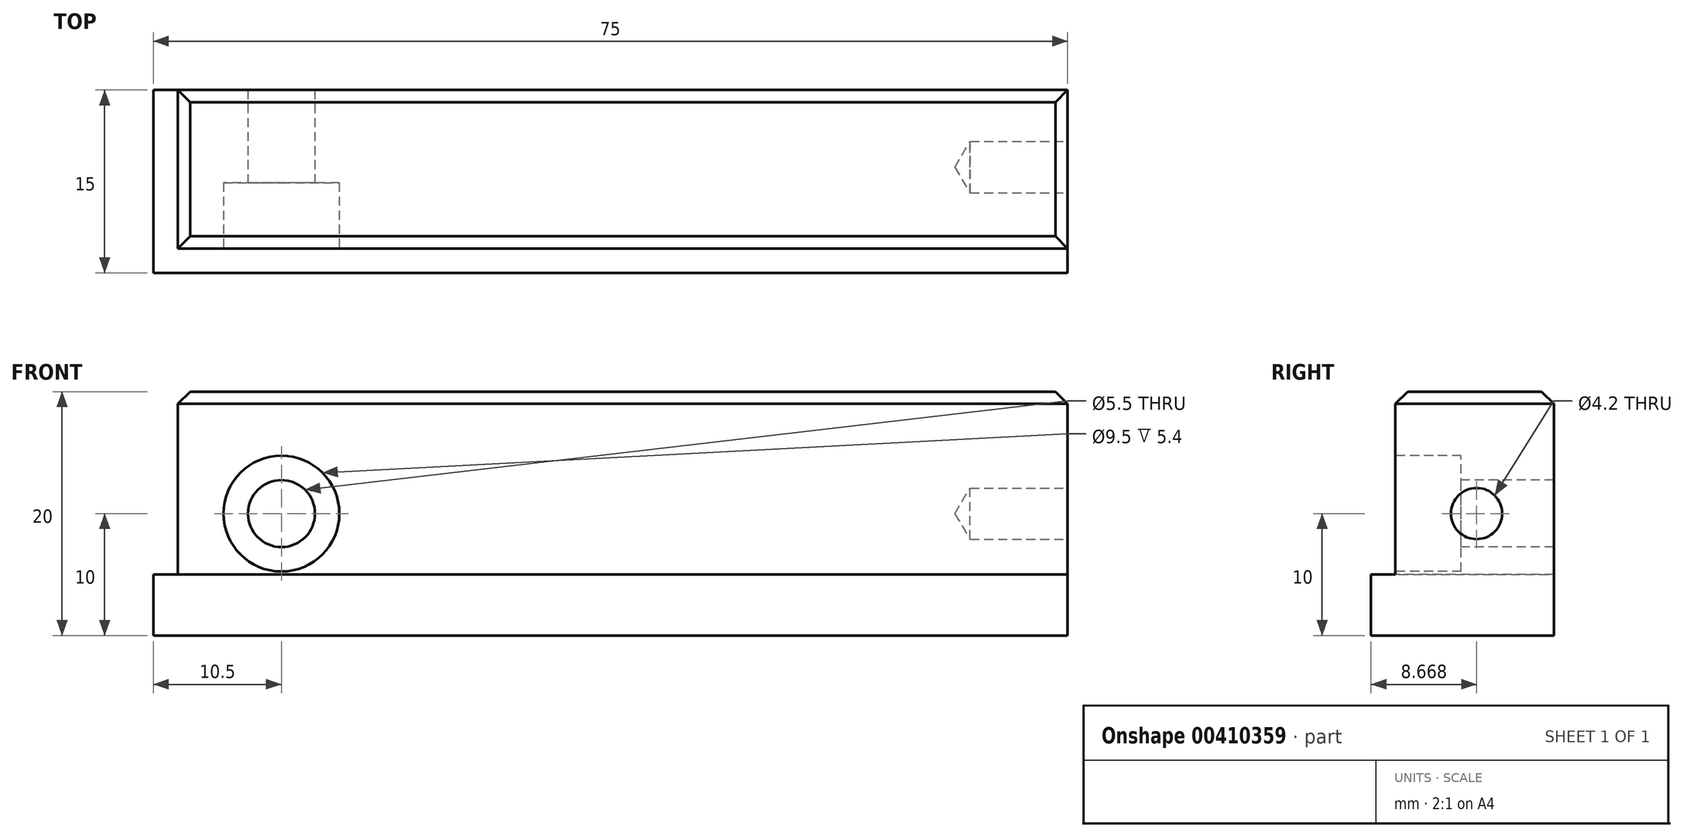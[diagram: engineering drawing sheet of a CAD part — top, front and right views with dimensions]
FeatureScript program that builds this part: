
annotation { "Feature Type Name" : "Feature", "Feature Type Description" : "" }
export const myFeature = defineFeature(function(context is Context, id is Id, definition is map)
    precondition{}
    {
        {
            var Q0;
            Q0=qCreatedBy(makeId("Front.planeOp"),FACE);
            var sketch = newSketch(context, id + "F0", { "sketchPlane" : qUnion([Q0])});
            skLineSegment(sketch, "E0.bottom", {"start": v(0, 0) * mm, "end": v(73, 0) * mm});
            skLineSegment(sketch, "E0.top", {"start": v(0, 20) * mm, "end": v(73, 20) * mm});
            skLineSegment(sketch, "E0.left", {"start": v(0, 0) * mm, "end": v(0, 20) * mm});
            skLineSegment(sketch, "E0.right", {"start": v(73, 0) * mm, "end": v(73, 20) * mm});
            skSolve(sketch);
        }
        {
            var Q0;
            Q0 = qSketchRegion(id + "F0", true);
            extrude(context, id + "F1", {"entities" : qUnion([Q0]), "depth" : 13 * mm});
        }
        {
            var Q0;
            Q0=makeQuery(id+"F1.opExtrude","CAP_FACE",FACE,{"disambiguationData":[OSD([sQuery(id+"F0.wireOp",EDGE,"E0.bottom"),sQuery(id+"F0.wireOp",EDGE,"E0.top"),sQuery(id+"F0.wireOp",EDGE,"E0.left"),sQuery(id+"F0.wireOp",EDGE,"E0.right")])],"isStart":false});
            var sketch = newSketch(context, id + "F2", { "sketchPlane" : qUnion([Q0])});
            skLineSegment(sketch, "E1.bottom", {"start": v(73, 0) * mm, "end": v(-2, 0) * mm});
            skLineSegment(sketch, "E1.top", {"start": v(73, 5) * mm, "end": v(-2, 5) * mm});
            skLineSegment(sketch, "E1.left", {"start": v(73, 0) * mm, "end": v(73, 5) * mm});
            skLineSegment(sketch, "E1.right", {"start": v(-2, 0) * mm, "end": v(-2, 5) * mm});
            skSolve(sketch);
        }
        {
            var Q0;
            Q0 = qSketchRegion(id + "F2", true);
            extrude(context, id + "F3", {"entities" : qUnion([Q0]), "operationType" : NewBodyOperationType.ADD, "depth" : 2 * mm});
        }
        {
            var Q0;
            Q0=makeQuery(id+"F1.opExtrude","SWEPT_FACE",FACE,{"disambiguationData":[OSD([sQuery(id+"F0.wireOp",EDGE,"E0.left")])]});
            var sketch = newSketch(context, id + "F4", { "sketchPlane" : qUnion([Q0])});
            skLineSegment(sketch, "E2.bottom", {"start": v(0, 0) * mm, "end": v(13, 0) * mm});
            skLineSegment(sketch, "E2.top", {"start": v(0, 5) * mm, "end": v(13, 5) * mm});
            skLineSegment(sketch, "E2.left", {"start": v(0, 0) * mm, "end": v(0, 5) * mm});
            skLineSegment(sketch, "E2.right", {"start": v(13, 0) * mm, "end": v(13, 5) * mm});
            skSolve(sketch);
        }
        {
            var Q0;
            Q0 = qSketchRegion(id + "F4", true);
            extrude(context, id + "F5", {"entities" : qUnion([Q0]), "operationType" : NewBodyOperationType.ADD, "depth" : 2 * mm});
        }
        {
            var Q0;
            Q0=makeQuery(id+"F1.opExtrude","CAP_FACE",FACE,{"disambiguationData":[OSD([sQuery(id+"F0.wireOp",EDGE,"E0.bottom"),sQuery(id+"F0.wireOp",EDGE,"E0.top"),sQuery(id+"F0.wireOp",EDGE,"E0.left"),sQuery(id+"F0.wireOp",EDGE,"E0.right")])],"isStart":false});
            var sketch = newSketch(context, id + "F6", { "sketchPlane" : qUnion([Q0])});
            skPoint(sketch, "E3", {"position": v(8.5, 10) * mm});
            skSolve(sketch);
        }
        {
            var Q0;
            Q0=sQuery(id+"F6.wireOp",VERTEX,"E3");
            var Q1;
            Q1=makeQuery(id+"F1.opExtrude","SWEPT_BODY",BODY,{"disambiguationData":[OSD([sQuery(id+"F0.wireOp",EDGE,"E0.bottom"),sQuery(id+"F0.wireOp",EDGE,"E0.top"),sQuery(id+"F0.wireOp",EDGE,"E0.left"),sQuery(id+"F0.wireOp",EDGE,"E0.right")])]});
            hole(context, id + "F7", {"style" : HoleStyle.C_BORE, "endStyle" : HoleEndStyle.THROUGH, "holeDiameter" : 5.5 * mm, "cBoreDiameter" : 9.5 * mm, "cBoreDepth" : 5.4 * mm, "isTappedThrough" : true, "tappedDepth" : 5 * mm, "tapClearance" : 3, "locations" : qUnion([Q0]), "scope" : qUnion([Q1])});
        }
        {
            var Q0;
            Q0=makeQuery(id+"F3.boolean.opBoolean","MERGE",FACE,{"derivedFrom":[makeQuery(id+"F1.opExtrude","SWEPT_FACE",FACE,{"disambiguationData":[OSD([sQuery(id+"F0.wireOp",EDGE,"E0.right")])]}),makeQuery(id+"F3.opExtrude","SWEPT_FACE",FACE,{"disambiguationData":[OSD([sQuery(id+"F2.wireOp",EDGE,"E1.left")])]})]});
            var sketch = newSketch(context, id + "F8", { "sketchPlane" : qUnion([Q0])});
            skPoint(sketch, "E4", {"position": v(-6.33, 10) * mm});
            skSolve(sketch);
        }
        {
            var Q0;
            Q0=sQuery(id+"F8.wireOp",VERTEX,"E4");
            var Q1;
            Q1=makeQuery(id+"F1.opExtrude","SWEPT_BODY",BODY,{"disambiguationData":[OSD([sQuery(id+"F0.wireOp",EDGE,"E0.bottom"),sQuery(id+"F0.wireOp",EDGE,"E0.top"),sQuery(id+"F0.wireOp",EDGE,"E0.left"),sQuery(id+"F0.wireOp",EDGE,"E0.right")])]});
            hole(context, id + "F9", {"style" : HoleStyle.SIMPLE, "endStyle" : HoleEndStyle.BLIND, "standardTappedOrClearance" : lookupTablePath({ "standard" : "ISO", "engagement" : "75%", "pitch" : "0.8 mm", "size" : "M5", "type" : "Tapped" }), "standardBlindInLast" : lookupTablePath({ "standard" : "ISO", "engagement" : "75%", "pitch" : "0.8 mm", "size" : "M5", "type" : "Tapped" }), "holeDiameter" : 4.2 * mm, "showTappedDepth" : true, "holeDepth" : 8 * mm, "isTappedThrough" : true, "tappedDepth" : 5.6 * mm, "tapClearance" : 3, "locations" : qUnion([Q0]), "scope" : qUnion([Q1]), "majorDiameter" : 5 * mm});
        }
        {
            var Q0;
            Q0=makeQuery(id+"F1.opExtrude","CAP_EDGE",EDGE,{"disambiguationData":[OSD([sQuery(id+"F0.wireOp",EDGE,"E0.top")])],"isStart":true});
            var Q1;
            Q1=makeQuery(id+"F1.opExtrude","CAP_EDGE",EDGE,{"disambiguationData":[OSD([sQuery(id+"F0.wireOp",EDGE,"E0.top")])],"isStart":false});
            var Q2;
            Q2=makeQuery(id+"F1.opExtrude","SWEPT_EDGE",EDGE,{"disambiguationData":[OSD([sQuery(id+"F0.wireOp",EDGE,"E0.top"),sQuery(id+"F0.wireOp",EDGE,"E0.left")])]});
            var Q3;
            Q3=makeQuery(id+"F1.opExtrude","SWEPT_EDGE",EDGE,{"disambiguationData":[OSD([sQuery(id+"F0.wireOp",EDGE,"E0.top"),sQuery(id+"F0.wireOp",EDGE,"E0.right")])]});
            chamfer(context, id + "F10", {"entities" : qUnion([Q0, Q1, Q2, Q3]), "width" : 1 * mm, "tangentPropagation" : true});
        }
    });
